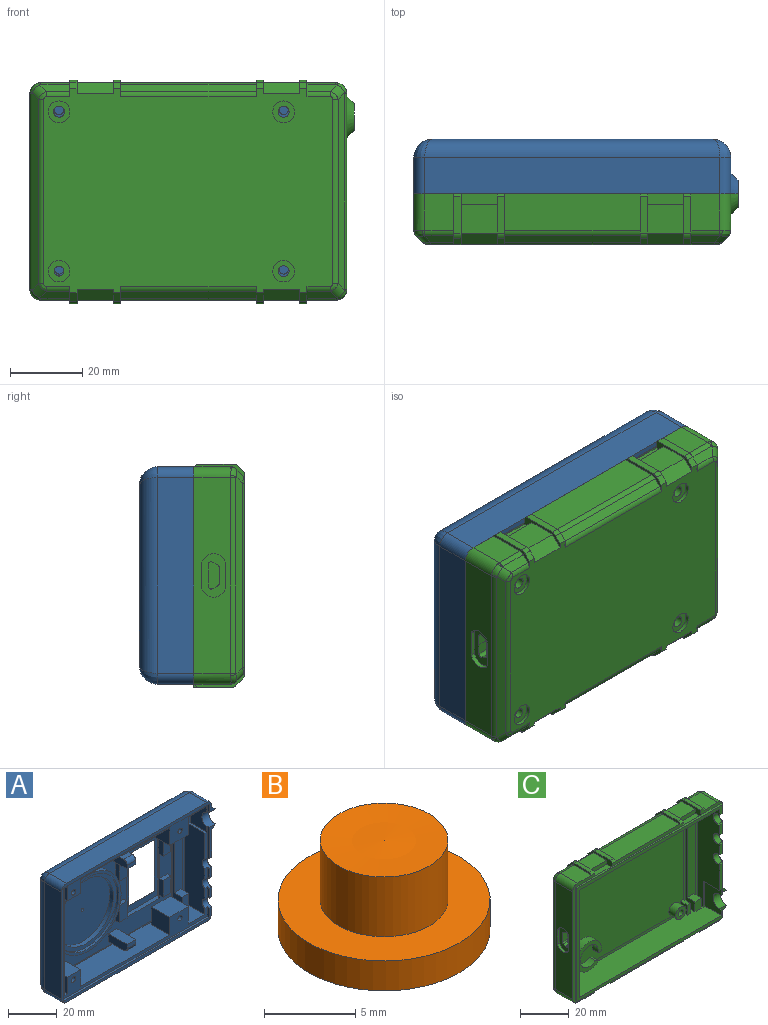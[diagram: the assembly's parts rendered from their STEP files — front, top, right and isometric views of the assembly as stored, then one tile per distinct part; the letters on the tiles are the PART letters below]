
ASSEMBLY  parts=3 mates=3
PART A: 134 faces, bbox 89.5x15x60 mm
  f0: plane 89.5x60mm, normal (0,-1,0), area 326.9mm2, adj f28,f29,f31,f46,f47,f50,f51,f56
  f1: plane 77.5x50mm, normal (0,1,0), area 3239.4mm2, adj f53,f113,f114,f115,f116,f122,f125,f126
  f2: plane 85x57mm, normal (0,-1,0), area 663.4mm2, adj f3,f4,f11,f12,f14,f15,f17,f18
  f3: plane 11x10.5mm, normal (0,0,-1), area 115.5mm2, adj f2,f8,f17,f112
  f4: plane 11x10.5mm, normal (0,0,1), area 115.5mm2, adj f2,f8,f18,f111
  f5: plane 11x2mm, normal (0,1,0), area 22mm2, adj f15,f16,f18,f111
  f6: plane 5x2mm, normal (0,-1,0), area 10mm2, adj f71,f72,f73,f75
  f7: plane 5x2mm, normal (0,-1,0), area 10mm2, adj f66,f67,f68,f70
  f8: plane 70.71x50mm, normal (0,-1,0), area 1324.2mm2, adj f3,f4,f10,f11,f12,f16,f17,f18
  f9: plane 32.22x20.2mm, normal (0,-1,0), area 258mm2, adj f10,f23,f92,f113,f114,f115,f116,f118
  f10: plane 20.2x2mm, normal (0,0,-1), area 39.9mm2, adj f8,f9,f92,f93,f117,f118
  f11: plane 10.5x7.6mm, normal (0,0,-1), area 79.8mm2, adj f2,f8,f83,f89,f91
  f12: plane 10.5x7.6mm, normal (0,0,1), area 79.8mm2, adj f2,f8,f13,f88,f90
  f13: plane 8.4x7.6mm, normal (0,1,0), area 18.3mm2, adj f12,f15,f16,f64,f88,f90
  f14: plane 81.5x12mm, normal (0,0,-1), area 782.7mm2, adj f2,f17,f26,f37,f65,f78,f83,f89
  f15: plane 81.5x12mm, normal (0,0,1), area 782.7mm2, adj f2,f5,f13,f18,f26,f37,f65,f88
  f16: plane 77.51x5.5mm, normal (0,0,-1), area 128.4mm2, adj f5,f8,f13,f24,f35,f39,f40,f41
  f17: plane 10.5x8.9mm, normal (-1,0,0), area 93.4mm2, adj f2,f3,f8,f14,f78
  f18: plane 10.5x8.9mm, normal (-1,0,0), area 93.4mm2, adj f2,f4,f5,f8,f15
  f19: plane 77.51x5.5mm, normal (0,0,1), area 128.4mm2, adj f8,f24,f35,f39,f43,f44,f52,f63
  f20: cylinder r=18mm len=36mm, axis (0,1,0), area 135.7mm2, adj f76,f77
  f21: cylinder r=19.25mm len=38.5mm, axis (0,1,0), area 326.6mm2, adj f8,f77
  f22: cylinder r=16mm len=32mm, axis (0,1,0), area 201.1mm2, adj f45,f76
  f23: plane 20.2x2mm, normal (0,0,1), area 39.9mm2, adj f8,f9,f92,f93,f117,f118
  f24: plane 50x1.3mm, normal (1,0,0), area 65mm2, adj f8,f16,f19,f52
  f25: plane 16.09x1.5mm, normal (0,-1,0), area 21.4mm2, adj f26,f48,f55,f57,f61,f62
  f26: plane 54x12mm, normal (-1,0,0), area 512.2mm2, adj f2,f14,f15,f25,f30,f36,f54,f55
  f27: plane 15.75x3.5mm, normal (0,-1,0), area 25.6mm2, adj f29,f48,f55,f57,f58
  f28: plane 4.39x1mm, normal (-1,0,0), area 4.3mm2, adj f0,f2,f47,f57
  f29: plane 54x10mm, normal (1,0,0), area 458.6mm2, adj f0,f27,f34,f49,f54,f55,f56,f58
  f30: plane 5.42x1.5mm, normal (0,-1,0), area 8.1mm2, adj f26,f32,f54,f55
  f31: plane 4.71x1mm, normal (-1,0,0), area 4.6mm2, adj f0,f2,f46,f56
  f32: plane 5.42x1mm, normal (-1,0,0), area 5.1mm2, adj f30,f34,f54,f55
  f33: plane 5.42x1mm, normal (-1,0,0), area 5.1mm2, adj f36,f49,f54,f56
  f34: plane 5x1.5mm, normal (0,-1,0), area 7.5mm2, adj f29,f32,f54,f55
  f35: plane 50x4.8mm, normal (0,-1,0), area 187.6mm2, adj f16,f19,f38,f39,f40,f42,f43,f63
  f36: plane 5.42x1.5mm, normal (0,-1,0), area 8.1mm2, adj f26,f33,f54,f56
  f37: plane 54x12mm, normal (1,0,0), area 648mm2, adj f2,f14,f15,f65
  f38: plane 4.5x3.8mm, normal (0,0,1), area 17.1mm2, adj f35,f39,f40,f41
  f39: plane 50x5.3mm, normal (-1,0,0), area 102.1mm2, adj f16,f19,f35,f38,f41,f42,f44,f52
  f40: plane 6.9x4.5mm, normal (1,0,0), area 31mm2, adj f16,f35,f38,f41
  f41: plane 6.9x3.8mm, normal (0,-1,0), area 26.2mm2, adj f16,f38,f39,f40
  f42: plane 4.5x3.8mm, normal (0,0,-1), area 17.1mm2, adj f35,f39,f43,f44
  f43: plane 6.9x4.5mm, normal (1,0,0), area 31mm2, adj f19,f35,f42,f44
  f44: plane 6.9x3.8mm, normal (0,-1,0), area 26.2mm2, adj f19,f39,f42,f43
  f45: plane 32x32mm, normal (0,-1,0), area 802.5mm2, adj f22,f53
  f46: plane 85x1mm, normal (0,0,1), area 85mm2, adj f0,f2,f31,f108
  f47: plane 85x1mm, normal (0,0,-1), area 85mm2, adj f0,f2,f28,f108
  f48: plane 16.09x1mm, normal (-1,0,0), area 15.9mm2, adj f25,f27,f55,f57
  f49: plane 5x1.5mm, normal (0,-1,0), area 7.5mm2, adj f29,f33,f54,f56
  f50: plane 81.5x10mm, normal (0,0,-1), area 815mm2, adj f0,f110,f120,f126
  f51: plane 81.5x10mm, normal (0,0,1), area 815mm2, adj f0,f109,f121,f125
  f52: plane 50x2mm, normal (0,-1,0), area 100mm2, adj f16,f19,f24,f39
  f53: cylinder r=0.75mm len=3mm, axis (0,-1,0), area 14.1mm2, adj f1,f45
  f54: cylinder r=2.5mm len=5mm, axis (1,0,0), area 20.5mm2, adj f26,f29,f30,f32,f33,f34,f36,f49
  f55: cylinder r=2.5mm len=5mm, axis (1,0,0), area 20.5mm2, adj f25,f26,f27,f29,f30,f32,f34,f48
  f56: cylinder r=2.5mm len=5mm, axis (1,0,0), area 20.5mm2, adj f0,f2,f26,f29,f31,f33,f36,f49
  f57: cylinder r=3.75mm len=7.5mm, axis (1,0,0), area 46.1mm2, adj f0,f2,f25,f27,f28,f48,f58,f62
  f58: cone r=3.75mm half-angle=45deg, axis (-1,0,0), area 42.2mm2, adj f0,f27,f29,f57
  f59: plane 9.5x1mm, normal (0,0,-1), area 9.5mm2, adj f2,f26,f60,f62
  f60: plane 12.73x1mm, normal (0,-1,0), area 12.7mm2, adj f26,f59,f61,f62
  f61: plane 9.5x1mm, normal (0,0,1), area 9.5mm2, adj f25,f26,f60,f62
  f62: plane 12.73x9.5mm, normal (-1,0,0), area 106.2mm2, adj f2,f25,f57,f59,f60,f61
  f63: plane 50x1mm, normal (1,0,0), area 50mm2, adj f16,f19,f35,f65
  f64: plane 50x1.5mm, normal (-1,0,0), area 75mm2, adj f8,f13,f16,f19,f65,f83
  f65: plane 81.5x54mm, normal (0,-1,0), area 525.5mm2, adj f14,f15,f16,f19,f26,f37,f63,f64
  f66: cylinder r=2mm len=5mm, axis (-1,0,0), area 15.7mm2, adj f7,f68,f69,f70
  f67: plane 11x5mm, normal (0,0,1), area 55mm2, adj f7,f8,f68,f70
  f68: plane 11x4mm, normal (1,0,0), area 43.1mm2, adj f7,f8,f66,f67,f69
  f69: plane 9x5mm, normal (0,0,-1), area 45mm2, adj f8,f66,f68,f70
  f70: plane 11x4mm, normal (-1,0,0), area 43.1mm2, adj f7,f8,f66,f67,f69
  f71: cylinder r=2mm len=5mm, axis (1,0,0), area 15.7mm2, adj f6,f73,f74,f75
  f72: plane 11x5mm, normal (0,0,-1), area 55mm2, adj f6,f8,f73,f75
  f73: plane 11x4mm, normal (-1,0,0), area 43.1mm2, adj f6,f8,f71,f72,f74
  f74: plane 9x5mm, normal (0,0,1), area 45mm2, adj f8,f71,f73,f75
  f75: plane 11x4mm, normal (1,0,0), area 43.1mm2, adj f6,f8,f71,f72,f74
  f76: plane 36x36mm, normal (0,-1,0), area 213.6mm2, adj f20,f22
  f77: plane 38.5x38.5mm, normal (0,-1,0), area 146.3mm2, adj f20,f21
  f78: plane 11x2mm, normal (0,1,0), area 22mm2, adj f14,f17,f19,f112
  f79: plane 2.5x2.5mm, normal (0,-1,0), area 4.9mm2, adj f80
  f80: cylinder r=1.25mm len=11mm, axis (0,1,0), area 86.4mm2, adj f2,f79
  f81: plane 2.5x2.5mm, normal (0,-1,0), area 4.9mm2, adj f82
  f82: cylinder r=1.25mm len=11mm, axis (0,1,0), area 86.4mm2, adj f2,f81
  f83: plane 7.6x7.1mm, normal (0,1,0), area 17.7mm2, adj f11,f14,f19,f64,f89,f91
  f84: plane 2.5x2.5mm, normal (0,-1,0), area 4.9mm2, adj f85
  f85: cylinder r=1.25mm len=11mm, axis (0,1,0), area 86.4mm2, adj f2,f84
  f86: plane 2.5x2.5mm, normal (0,-1,0), area 4.9mm2, adj f87
  f87: cylinder r=1.25mm len=11mm, axis (0,1,0), area 86.4mm2, adj f2,f86
  f88: plane 10.5x8.4mm, normal (-1,0,0), area 88.2mm2, adj f2,f12,f13,f15
  f89: plane 10.5x7.1mm, normal (-1,0,0), area 74.5mm2, adj f2,f11,f14,f83
  f90: plane 10.5x8.4mm, normal (1,0,0), area 88.2mm2, adj f2,f8,f12,f13,f15
  f91: plane 10.5x7.1mm, normal (1,0,0), area 74.5mm2, adj f2,f8,f11,f14,f83
  f92: plane 32.22x2mm, normal (1,0,0), area 64.4mm2, adj f8,f9,f10,f23
  f93: plane 32.22x2.5mm, normal (-1,0,0), area 50.1mm2, adj f8,f10,f23,f94,f96,f97,f99,f117
  f94: plane 4.5x2mm, normal (0,0,1), area 9mm2, adj f8,f93,f95,f96
  f95: plane 8.5x2mm, normal (1,0,0), area 17mm2, adj f8,f94,f96,f131
  f96: plane 8.5x4.5mm, normal (0,-1,0), area 38.2mm2, adj f93,f94,f95,f131
  f97: plane 4.5x2mm, normal (0,0,-1), area 9mm2, adj f8,f93,f98,f99
  f98: plane 8.5x2mm, normal (1,0,0), area 17mm2, adj f8,f97,f99,f132
  f99: plane 8.5x4.5mm, normal (0,-1,0), area 38.2mm2, adj f93,f97,f98,f132
  f100: plane 8.5x2mm, normal (1,0,0), area 17mm2, adj f8,f101,f103,f130
  f101: plane 4.61x2mm, normal (0,0,1), area 9.2mm2, adj f8,f100,f102,f103
  f102: plane 8.5x2mm, normal (-1,0,0), area 17mm2, adj f8,f101,f103,f130
  f103: plane 8.5x4.61mm, normal (0,-1,0), area 39.2mm2, adj f100,f101,f102,f130
  f104: plane 4.61x2mm, normal (0,0,-1), area 9.2mm2, adj f8,f105,f106,f107
  f105: plane 8.5x2mm, normal (1,0,0), area 17mm2, adj f8,f104,f107,f133
  f106: plane 8.5x2mm, normal (-1,0,0), area 17mm2, adj f8,f104,f107,f133
  f107: plane 8.5x4.61mm, normal (0,-1,0), area 39.2mm2, adj f104,f105,f106,f133
  f108: plane 57x1mm, normal (1,0,0), area 57mm2, adj f0,f2,f46,f47
  f109: cylinder r=3mm len=10mm, axis (0,1,0), area 47.1mm2, adj f0,f29,f51,f127
  f110: cylinder r=3mm len=10mm, axis (0,-1,0), area 47.1mm2, adj f0,f29,f50,f128
  f111: plane 10.5x8.9mm, normal (1,0,0), area 93.4mm2, adj f2,f4,f5,f8,f15
  f112: plane 10.5x8.9mm, normal (1,0,0), area 93.4mm2, adj f2,f3,f8,f14,f78
  f113: cylinder r=3mm len=31.29mm, axis (0,0,1), area 89.3mm2, adj f1,f9,f114,f115
  f114: cylinder r=3mm len=20.25mm, axis (1,0,0), area 54.6mm2, adj f1,f9,f113,f116
  f115: cylinder r=3mm len=20.25mm, axis (-1,0,0), area 54.6mm2, adj f1,f9,f113,f116
  f116: cylinder r=3mm len=31.29mm, axis (0,0,-1), area 89.3mm2, adj f1,f9,f114,f115
  f117: plane 32.22x1mm, normal (0,1,0), area 32.2mm2, adj f10,f23,f93,f118
  f118: plane 32.22x1.5mm, normal (-1,0,0), area 48.3mm2, adj f9,f10,f23,f117
  f119: plane 54x10mm, normal (-1,0,0), area 540mm2, adj f0,f120,f121,f122
  f120: cylinder r=3mm len=10mm, axis (0,1,0), area 47.1mm2, adj f0,f50,f119,f124
  f121: cylinder r=3mm len=10mm, axis (0,-1,0), area 47.1mm2, adj f0,f51,f119,f123
  f122: cylinder r=5mm len=54mm, axis (0,0,-1), area 412.7mm2, adj f1,f119,f123,f124
  f123: bspline ~6.03x5mm, area 24.5mm2, adj f121,f122,f125
  f124: bspline ~6.03x5mm, area 24.5mm2, adj f120,f122,f126
  f125: cylinder r=5mm len=81.5mm, axis (-1,0,0), area 628.7mm2, adj f1,f51,f123,f127
  f126: cylinder r=5mm len=81.5mm, axis (1,0,0), area 628.7mm2, adj f1,f50,f124,f128
  f127: bspline ~6.03x5mm, area 24.5mm2, adj f109,f125,f129
  f128: bspline ~6.03x5mm, area 24.5mm2, adj f110,f126,f129
  f129: cylinder r=5mm len=54mm, axis (0,0,1), area 412.7mm2, adj f1,f29,f127,f128
  f130: plane 4.61x2mm, normal (0,0,-1), area 9.2mm2, adj f8,f100,f102,f103
  f131: plane 4.5x2mm, normal (0,0,-1), area 9mm2, adj f8,f93,f95,f96
  f132: plane 4.5x2mm, normal (0,0,1), area 9mm2, adj f8,f93,f98,f99
  f133: plane 4.61x2mm, normal (0,0,1), area 9.2mm2, adj f8,f105,f106,f107
PART B: 7 faces, bbox 11.6x11.6x6 mm
  f0: plane 4x4mm, normal (0,0,-1), area 12.6mm2, adj f6
  f1: torus R=1.75mm, axis (0,0,1), area 38.5mm2, adj f2
  f2: cylinder r=3.5mm len=7mm, axis (0,0,1), area 88mm2, adj f1,f3
  f3: plane 11.6x11.6mm, normal (0,0,1), area 67.2mm2, adj f2,f4
  f4: cylinder r=5.8mm len=11.6mm, axis (0,0,1), area 72.9mm2, adj f3,f5
  f5: plane 11.6x11.6mm, normal (0,0,-1), area 93.1mm2, adj f4,f6
  f6: cylinder r=2mm len=4mm, axis (0,0,1), area 50.3mm2, adj f0,f5
PART C: 234 faces, bbox 89.5x15x61.7 mm
  f0: cylinder r=0.8mm len=3.7mm, axis (1,0,0), area 6mm2, adj f1,f8,f9,f233
  f1: plane 3.7x2.97mm, normal (0,1,-0.01), area 11mm2, adj f0,f2,f9,f233
  f2: plane 3.7x2.96mm, normal (0,1,0), area 10.9mm2, adj f1,f3,f9,f233
  f3: cylinder r=0.8mm len=3.7mm, axis (1,0,0), area 6.1mm2, adj f2,f4,f9,f233
  f4: plane 3.7x1.37mm, normal (0,-0.45,0.89), area 5.7mm2, adj f3,f5,f9,f233
  f5: cylinder r=0.81mm len=3.7mm, axis (1,0,0), area 3.3mm2, adj f4,f6,f9,f233
  f6: plane 4.51x3.7mm, normal (0,-1,0), area 16.7mm2, adj f5,f7,f9,f233
  f7: cylinder r=0.83mm len=3.7mm, axis (1,0,0), area 3.2mm2, adj f6,f8,f9,f233
  f8: plane 3.7x1.37mm, normal (0,-0.46,-0.89), area 5.7mm2, adj f0,f7,f9,f233
  f9: plane 14x9.5mm, normal (1,0,0), area 112.9mm2, adj f0,f1,f2,f3,f4,f5,f6,f7
  f10: plane 70.7x50mm, normal (0,-1,0), area 3334.4mm2, adj f9,f34,f61,f68,f72,f77,f82,f139
  f11: plane 14x2mm, normal (0,-1,0), area 28mm2, adj f9,f13,f14,f225
  f12: plane 5.01x2.01mm, normal (0,0,1), area 10mm2, adj f9,f14,f226,f227,f228
  f13: plane 4.01x2.01mm, normal (0,0,1), area 8mm2, adj f9,f11,f14,f228
  f14: plane 54x13mm, normal (1,0,0), area 555mm2, adj f11,f12,f13,f22,f55,f56,f225,f227
  f15: plane 5.5x4.8mm, normal (0,0,1), area 21.9mm2, adj f17,f76,f78,f79,f223,f227
  f16: plane 5.5x4.8mm, normal (0,0,-1), area 21.9mm2, adj f17,f78,f80,f83,f223,f227
  f17: plane 50x4.8mm, normal (0,-1,0), area 202mm2, adj f15,f16,f75,f76,f78,f80,f81,f223
  f18: plane 54x13mm, normal (-1,0,0), area 534mm2, adj f19,f22,f55,f56,f84,f85,f86,f151
  f19: plane 15.75x1.5mm, normal (0,-1,0), area 20.9mm2, adj f18,f23,f153,f154,f220,f222
  f20: cylinder r=3.75mm len=7.5mm, axis (1,0,0), area 47.1mm2, adj f21,f23,f27,f31,f219,f222
  f21: plane 1x0.5mm, normal (0,0,1), area 0.5mm2, adj f20,f22,f150,f222
  f22: plane 84.5x57mm, normal (0,-1,0), area 340.4mm2, adj f14,f18,f21,f55,f56,f146,f147,f148
  f23: plane 1x0.5mm, normal (0,0,-1), area 0.5mm2, adj f19,f20,f154,f222
  f24: plane 54x10.17mm, normal (1,0,0), area 467.9mm2, adj f27,f29,f30,f31,f32,f84,f85,f86
  f25: plane 10x8mm, normal (0,0,-1), area 80mm2, adj f40,f125,f132,f213
  f26: plane 10x8mm, normal (0,0,-1), area 80mm2, adj f41,f117,f120,f211
  f27: plane 15x5.75mm, normal (0,-1,0), area 25.9mm2, adj f20,f24,f59,f93,f116,f117,f149,f150
  f28: plane 41.5x1.5mm, normal (0,-1,0), area 62.2mm2, adj f38,f120,f121,f131,f132,f149
  f29: plane 5x1.5mm, normal (0,-1,0), area 7.5mm2, adj f24,f84,f85,f160
  f30: plane 5x1.5mm, normal (0,-1,0), area 7.5mm2, adj f24,f85,f86,f157
  f31: plane 15.75x3.5mm, normal (0,-1,0), area 25.6mm2, adj f20,f24,f86,f154,f219
  f32: plane 13x7mm, normal (0,-1,0), area 26.3mm2, adj f24,f57,f84,f97,f99,f100,f101,f146
  f33: plane 60x13mm, normal (0,-1,0), area 120.6mm2, adj f42,f45,f58,f91,f95,f108,f125,f126
  f34: cylinder r=3mm len=6mm, axis (0,1,0), area 74.8mm2, adj f10,f65,f139,f143,f144
  f35: plane 10x8mm, normal (0,0,1), area 80mm2, adj f44,f108,f111,f137
  f36: plane 10x8mm, normal (0,0,1), area 80mm2, adj f49,f100,f103,f135
  f37: plane 41.5x1.5mm, normal (0,-1,0), area 62.2mm2, adj f47,f103,f111,f147,f216,f217
  f38: plane 37.5x10.17mm, normal (0,0,-1), area 381.4mm2, adj f28,f122,f130,f191
  f39: plane 37.5x1.83mm, normal (0,0.71,-0.71), area 97mm2, adj f122,f130,f191,f192
  f40: plane 10x3mm, normal (0,0.71,-0.71), area 42.4mm2, adj f25,f54,f125,f132
  f41: plane 10x3mm, normal (0,0.71,-0.71), area 42.4mm2, adj f26,f54,f117,f120
  f42: plane 10.17x8mm, normal (0,0,-1), area 81.4mm2, adj f33,f91,f127,f172
  f43: plane 8.26x1.83mm, normal (0,0.71,-0.71), area 19.1mm2, adj f92,f127,f172,f173,f186
  f44: plane 10x3mm, normal (0,0.71,0.71), area 42.4mm2, adj f35,f54,f108,f111
  f45: plane 10.17x8mm, normal (0,0,1), area 81.4mm2, adj f33,f95,f107,f180
  f46: plane 8.26x1.83mm, normal (0,0.71,0.71), area 19.1mm2, adj f96,f107,f179,f180,f190
  f47: plane 37.5x10.17mm, normal (0,0,1), area 381.4mm2, adj f37,f104,f112,f198
  f48: plane 37.5x1.83mm, normal (0,0.71,0.71), area 97mm2, adj f104,f112,f197,f198
  f49: plane 10x3mm, normal (0,0.71,0.71), area 42.4mm2, adj f36,f54,f100,f103
  f50: cylinder r=3mm len=6mm, axis (0,1,0), area 18.8mm2, adj f54,f74
  f51: cylinder r=3mm len=6mm, axis (0,1,0), area 18.8mm2, adj f54,f70
  f52: cylinder r=3mm len=6mm, axis (0,1,0), area 18.8mm2, adj f54,f66
  f53: cylinder r=3mm len=6mm, axis (0,1,0), area 18.8mm2, adj f54,f63
  f54: plane 79.84x56.41mm, normal (0,1,0), area 4131.5mm2, adj f40,f41,f44,f49,f50,f51,f52,f53
  f55: plane 81.5x13mm, normal (0,0,-1), area 1059.5mm2, adj f14,f18,f22,f227
  f56: plane 82.5x13mm, normal (0,0,1), area 1069mm2, adj f14,f18,f22,f221,f222,f227
  f57: plane 10.17x8mm, normal (0,0,1), area 81.4mm2, adj f32,f97,f99,f171
  f58: plane 54x10.17mm, normal (-1,0,0), area 479.4mm2, adj f33,f91,f95,f176,f229,f230,f231,f232
  f59: plane 10.17x8mm, normal (0,0,-1), area 81.4mm2, adj f27,f93,f115,f163
  f60: cylinder r=1.35mm len=6mm, axis (0,1,0), area 50.9mm2, adj f62,f63
  f61: cylinder r=3mm len=6mm, axis (0,1,0), area 75.4mm2, adj f10,f62
  f62: plane 6x6mm, normal (0,-1,0), area 22.5mm2, adj f60,f61
  f63: plane 6x6mm, normal (0,1,0), area 22.5mm2, adj f53,f60
  f64: cylinder r=1.5mm len=6mm, axis (0,1,0), area 56.5mm2, adj f65,f66
  f65: plane 6x6mm, normal (0,-1,0), area 21.2mm2, adj f34,f64
  f66: plane 6x6mm, normal (0,1,0), area 21.2mm2, adj f52,f64
  f67: cylinder r=1.5mm len=6mm, axis (0,1,0), area 56.5mm2, adj f69,f70
  f68: cylinder r=3mm len=6mm, axis (0,1,0), area 75.4mm2, adj f10,f69
  f69: plane 6x6mm, normal (0,-1,0), area 21.2mm2, adj f67,f68
  f70: plane 6x6mm, normal (0,1,0), area 21.2mm2, adj f51,f67
  f71: cylinder r=1.5mm len=6mm, axis (0,1,0), area 56.5mm2, adj f73,f74
  f72: cylinder r=3mm len=6mm, axis (0,1,0), area 75.4mm2, adj f10,f73
  f73: plane 6x6mm, normal (0,-1,0), area 21.2mm2, adj f71,f72
  f74: plane 6x6mm, normal (0,1,0), area 21.2mm2, adj f50,f71
  f75: plane 4.5x3.8mm, normal (0,0,-1), area 17.1mm2, adj f17,f76,f78,f79
  f76: plane 5x4.5mm, normal (1,0,0), area 22.5mm2, adj f15,f17,f75,f79
  f77: plane 70.7x5mm, normal (0,0,1), area 78.3mm2, adj f10,f204,f205,f206,f226,f227
  f78: plane 50x5.5mm, normal (-1,0,0), area 95mm2, adj f15,f16,f17,f75,f79,f81,f83,f227
  f79: plane 5x3.8mm, normal (0,-1,0), area 19mm2, adj f15,f75,f76,f78
  f80: plane 5x4.5mm, normal (1,0,0), area 22.5mm2, adj f16,f17,f81,f83
  f81: plane 4.5x3.8mm, normal (0,0,1), area 17.1mm2, adj f17,f78,f80,f83
  f82: plane 70.7x5mm, normal (0,0,-1), area 78.3mm2, adj f10,f204,f208,f209,f224,f227
  f83: plane 5x3.8mm, normal (0,-1,0), area 19mm2, adj f16,f78,f80,f81
  f84: cylinder r=2.5mm len=5mm, axis (1,0,0), area 23.6mm2, adj f18,f24,f29,f32,f151,f161
  f85: cylinder r=2.5mm len=5mm, axis (1,0,0), area 23.6mm2, adj f18,f24,f29,f30,f155,f159
  f86: cylinder r=2.5mm len=5mm, axis (1,0,0), area 23.6mm2, adj f18,f24,f30,f31,f153,f156
  f87: plane 8.26x1.83mm, normal (0,0.71,-0.71), area 19.1mm2, adj f94,f115,f163,f164,f181
  f88: plane 54.52x1.83mm, normal (-0.71,0.71,0), area 136.4mm2, adj f92,f96,f175,f176,f177,f188
  f89: plane 54.52x1.83mm, normal (0.71,0.71,0), area 136.4mm2, adj f94,f98,f166,f167,f168,f183
  f90: plane 8.26x1.83mm, normal (0,0.71,0.71), area 19.1mm2, adj f98,f99,f170,f171,f185
  f91: cylinder r=3mm len=10.21mm, axis (0,1,0), area 48.1mm2, adj f33,f42,f58,f173,f174,f175
  f92: cylinder r=3mm len=3.92mm, axis (-0.58,-0.58,-0.58), area 9.8mm2, adj f43,f88,f174,f187
  f93: cylinder r=3mm len=10.21mm, axis (0,-1,0), area 48.1mm2, adj f24,f27,f59,f164,f165,f166
  f94: cylinder r=3mm len=3.92mm, axis (0.58,-0.58,-0.58), area 9.8mm2, adj f87,f89,f165,f182
  f95: cylinder r=3mm len=10.21mm, axis (0,-1,0), area 48.1mm2, adj f33,f45,f58,f177,f178,f179
  f96: cylinder r=3mm len=3.92mm, axis (0.58,0.58,-0.58), area 9.8mm2, adj f46,f88,f178,f189
  f97: cylinder r=3mm len=10.21mm, axis (0,1,0), area 48.1mm2, adj f24,f32,f57,f168,f169,f170
  f98: cylinder r=3mm len=3.92mm, axis (-0.58,0.58,-0.58), area 9.8mm2, adj f89,f90,f169,f184
  f99: plane 14x4.83mm, normal (1,0,0), area 14.1mm2, adj f32,f54,f57,f90,f101,f102,f171,f185
  f100: plane 14x4mm, normal (-1,0,0), area 19.9mm2, adj f32,f36,f49,f54,f101,f102,f135,f136
  f101: plane 10.17x2mm, normal (0,0,1), area 20.3mm2, adj f32,f99,f100,f202
  f102: plane 2.41x2.41mm, normal (0,0.71,0.71), area 6.8mm2, adj f54,f99,f100,f202
  f103: plane 14x4mm, normal (1,0,0), area 19.4mm2, adj f36,f37,f49,f54,f105,f106,f135,f136
  f104: plane 14x4.83mm, normal (-1,0,0), area 13.6mm2, adj f47,f48,f54,f105,f106,f197,f198,f201
  f105: plane 9.17x2mm, normal (0,0,1), area 18.3mm2, adj f103,f104,f201,f216
  f106: plane 2.41x2.41mm, normal (0,0.71,0.71), area 6.8mm2, adj f54,f103,f104,f201
  f107: plane 14x4.83mm, normal (-1,0,0), area 13.6mm2, adj f45,f46,f54,f109,f110,f180,f190,f199
  f108: plane 14x4mm, normal (1,0,0), area 19.4mm2, adj f33,f35,f44,f54,f109,f110,f137,f138
  f109: plane 9.17x2mm, normal (0,0,1), area 18.3mm2, adj f107,f108,f199,f218
  f110: plane 2.41x2.41mm, normal (0,0.71,0.71), area 6.8mm2, adj f54,f107,f108,f199
  f111: plane 14x4mm, normal (-1,0,0), area 19.4mm2, adj f35,f37,f44,f54,f113,f114,f137,f138
  f112: plane 14x4.83mm, normal (1,0,0), area 13.6mm2, adj f47,f48,f54,f113,f114,f197,f198,f200
  f113: plane 9.17x2mm, normal (0,0,1), area 18.3mm2, adj f111,f112,f200,f217
  f114: plane 2.41x2.41mm, normal (0,0.71,0.71), area 6.8mm2, adj f54,f111,f112,f200
  f115: plane 14x4.54mm, normal (1,0,0), area 11.6mm2, adj f54,f59,f87,f116,f118,f119,f163,f181
  f116: plane 2x0.71mm, normal (0,-0.71,-0.71), area 2mm2, adj f27,f115,f117,f118
  f117: plane 14x3.71mm, normal (-1,0,0), area 17.4mm2, adj f26,f27,f41,f54,f116,f118,f119,f196
  f118: plane 10.17x2mm, normal (0,0,-1), area 20.3mm2, adj f115,f116,f117,f196
  f119: plane 2x1.71mm, normal (0,0.71,-0.71), area 4.8mm2, adj f54,f115,f117,f196
  f120: plane 14x3.71mm, normal (1,0,0), area 17.4mm2, adj f26,f28,f41,f54,f121,f123,f124,f193
  f121: plane 2x0.71mm, normal (0,-0.71,-0.71), area 2mm2, adj f28,f120,f122,f123
  f122: plane 14x4.54mm, normal (-1,0,0), area 11.6mm2, adj f38,f39,f54,f121,f123,f124,f191,f192
  f123: plane 10.17x2mm, normal (0,0,-1), area 20.3mm2, adj f120,f121,f122,f193
  f124: plane 2x1.71mm, normal (0,0.71,-0.71), area 4.8mm2, adj f54,f120,f122,f193
  f125: plane 14x3.71mm, normal (1,0,0), area 17.4mm2, adj f25,f33,f40,f54,f126,f128,f129,f194
  f126: plane 2x0.71mm, normal (0,-0.71,-0.71), area 2mm2, adj f33,f125,f127,f128
  f127: plane 14x4.54mm, normal (-1,0,0), area 11.6mm2, adj f42,f43,f54,f126,f128,f129,f172,f186
  f128: plane 10.17x2mm, normal (0,0,-1), area 20.3mm2, adj f125,f126,f127,f194
  f129: plane 2x1.71mm, normal (0,0.71,-0.71), area 4.8mm2, adj f54,f125,f127,f194
  f130: plane 14x4.54mm, normal (1,0,0), area 11.6mm2, adj f38,f39,f54,f131,f133,f134,f191,f192
  f131: plane 2x0.71mm, normal (0,-0.71,-0.71), area 2mm2, adj f28,f130,f132,f133
  f132: plane 14x3.71mm, normal (-1,0,0), area 17.4mm2, adj f25,f28,f40,f54,f131,f133,f134,f195
  f133: plane 10.17x2mm, normal (0,0,-1), area 20.3mm2, adj f130,f131,f132,f195
  f134: plane 2x1.71mm, normal (0,0.71,-0.71), area 4.8mm2, adj f54,f130,f132,f195
  f135: plane 10x2mm, normal (0,-1,0), area 20mm2, adj f36,f100,f103,f136
  f136: plane 10x3mm, normal (0,0,1), area 30mm2, adj f100,f103,f135,f145
  f137: plane 10x2mm, normal (0,-1,0), area 20mm2, adj f35,f108,f111,f138
  f138: plane 10x3mm, normal (0,0,1), area 30mm2, adj f108,f111,f137,f152
  f139: cylinder r=7.2mm len=11.72mm, axis (0,1,0), area 48.7mm2, adj f10,f34,f140,f144
  f140: plane 3.5x1.85mm, normal (0.45,0,0.89), area 7.2mm2, adj f10,f139,f141,f144
  f141: cylinder r=5.25mm len=10.5mm, axis (0,1,0), area 103.1mm2, adj f10,f140,f142,f144
  f142: plane 3.5x1.98mm, normal (0,0,-1), area 6.9mm2, adj f10,f141,f143,f144
  f143: cylinder r=7.2mm len=14.4mm, axis (0,1,0), area 93.5mm2, adj f10,f34,f142,f144
  f144: plane 14.4x14.4mm, normal (0,-1,0), area 68.5mm2, adj f34,f139,f140,f141,f142,f143
  f145: plane 10x0.5mm, normal (0,1,0), area 5mm2, adj f100,f103,f136,f147
  f146: plane 4.5x1mm, normal (1,0,0), area 4.5mm2, adj f22,f32,f147,f151
  f147: plane 84.5x1mm, normal (0,0,1), area 84.5mm2, adj f22,f32,f33,f37,f145,f146,f148,f152
  f148: plane 57x1mm, normal (-1,0,0), area 57mm2, adj f22,f33,f147,f149
  f149: plane 84.5x1mm, normal (0,0,-1), area 84.5mm2, adj f22,f27,f28,f33,f148,f150,f210,f214
  f150: plane 4.25x1mm, normal (1,0,0), area 4.2mm2, adj f21,f22,f27,f149
  f151: plane 1.5x1mm, normal (0,0,-1), area 1.5mm2, adj f18,f22,f84,f146
  f152: plane 10x0.5mm, normal (0,1,0), area 5mm2, adj f108,f111,f138,f147
  f153: plane 1.5x1mm, normal (0,0,1), area 1.5mm2, adj f18,f19,f86,f154
  f154: plane 15.75x1mm, normal (1,0,0), area 15.7mm2, adj f19,f23,f31,f153
  f155: plane 1.5x1mm, normal (0,0,1), area 1.5mm2, adj f18,f85,f157,f158
  f156: plane 1.5x1mm, normal (0,0,-1), area 1.5mm2, adj f18,f86,f157,f158
  f157: plane 5x1mm, normal (1,0,0), area 5mm2, adj f30,f155,f156,f158
  f158: plane 5x1.5mm, normal (0,-1,0), area 7.5mm2, adj f18,f155,f156,f157
  f159: plane 1.5x1mm, normal (0,0,-1), area 1.5mm2, adj f18,f85,f160,f162
  f160: plane 5x1mm, normal (1,0,0), area 5mm2, adj f29,f159,f161,f162
  f161: plane 1.5x1mm, normal (0,0,1), area 1.5mm2, adj f18,f84,f160,f162
  f162: plane 5x1.5mm, normal (0,-1,0), area 7.5mm2, adj f18,f159,f160,f161
  f163: cylinder r=2mm len=8mm, axis (1,0,0), area 12.6mm2, adj f59,f87,f115,f164
  f164: bspline ~1.46x0.9mm, area 0.9mm2, adj f87,f93,f163,f165
  f165: bspline ~3x3mm, area 6mm2, adj f93,f94,f164,f166
  f166: bspline ~1.46x0.9mm, area 0.9mm2, adj f89,f93,f165,f167
  f167: cylinder r=2mm len=54mm, axis (0,0,1), area 84.8mm2, adj f24,f89,f166,f168
  f168: bspline ~1.46x1.03mm, area 0.9mm2, adj f89,f97,f167,f169
  f169: bspline ~3x3mm, area 6mm2, adj f97,f98,f168,f170
  f170: bspline ~1.46x1.42mm, area 0.9mm2, adj f90,f97,f169,f171
  f171: cylinder r=2mm len=8mm, axis (-1,0,0), area 12.6mm2, adj f57,f90,f99,f170
  f172: cylinder r=2mm len=8mm, axis (1,0,0), area 12.6mm2, adj f42,f43,f127,f173
  f173: bspline ~1.46x1.03mm, area 0.9mm2, adj f43,f91,f172,f174
  f174: bspline ~3x3mm, area 6mm2, adj f91,f92,f173,f175
  f175: bspline ~1.46x1.42mm, area 0.9mm2, adj f88,f91,f174,f176
  f176: cylinder r=2mm len=54mm, axis (0,0,-1), area 84.8mm2, adj f58,f88,f175,f177
  f177: bspline ~1.46x0.9mm, area 0.9mm2, adj f88,f95,f176,f178
  f178: bspline ~3x3mm, area 6mm2, adj f95,f96,f177,f179
  f179: bspline ~1.46x0.9mm, area 0.9mm2, adj f46,f95,f178,f180
  f180: cylinder r=2mm len=8mm, axis (-1,0,0), area 12.6mm2, adj f45,f46,f107,f179
  f181: cylinder r=2mm len=6.46mm, axis (-1,0,0), area 10.2mm2, adj f54,f87,f115,f182
  f182: bspline ~2.12x2.12mm, area 2.9mm2, adj f54,f94,f181,f183
  f183: cylinder r=2mm len=50.93mm, axis (0,0,1), area 80mm2, adj f54,f89,f182,f184
  f184: bspline ~2.12x2.12mm, area 2.9mm2, adj f54,f98,f183,f185
  f185: cylinder r=2mm len=6.46mm, axis (-1,0,0), area 10.2mm2, adj f54,f90,f99,f184
  f186: cylinder r=2mm len=6.46mm, axis (-1,0,0), area 10.2mm2, adj f43,f54,f127,f187
  f187: bspline ~2.12x2.12mm, area 2.9mm2, adj f54,f92,f186,f188
  f188: cylinder r=2mm len=50.93mm, axis (0,0,1), area 80mm2, adj f54,f88,f187,f189
  f189: bspline ~2.12x2.12mm, area 2.9mm2, adj f54,f96,f188,f190
  f190: cylinder r=2mm len=6.46mm, axis (-1,0,0), area 10.2mm2, adj f46,f54,f107,f189
  f191: cylinder r=2mm len=37.5mm, axis (1,0,0), area 58.9mm2, adj f38,f39,f122,f130
  f192: cylinder r=2mm len=37.5mm, axis (-1,0,0), area 58.9mm2, adj f39,f54,f122,f130
  f193: cylinder r=2mm len=2mm, axis (1,0,0), area 3.1mm2, adj f120,f122,f123,f124
  f194: cylinder r=2mm len=2mm, axis (1,0,0), area 3.1mm2, adj f125,f127,f128,f129
  f195: cylinder r=2mm len=2mm, axis (1,0,0), area 3.1mm2, adj f130,f132,f133,f134
  f196: cylinder r=2mm len=2mm, axis (1,0,0), area 3.1mm2, adj f115,f117,f118,f119
  f197: cylinder r=2mm len=37.5mm, axis (-1,0,0), area 58.9mm2, adj f48,f54,f104,f112
  f198: cylinder r=2mm len=37.5mm, axis (-1,0,0), area 58.9mm2, adj f47,f48,f104,f112
  f199: cylinder r=2mm len=2mm, axis (-1,0,0), area 3.1mm2, adj f107,f108,f109,f110
  f200: cylinder r=2mm len=2mm, axis (-1,0,0), area 3.1mm2, adj f111,f112,f113,f114
  f201: cylinder r=2mm len=2mm, axis (-1,0,0), area 3.1mm2, adj f103,f104,f105,f106
  f202: cylinder r=2mm len=2mm, axis (-1,0,0), area 3.1mm2, adj f99,f100,f101,f102
  f203: plane 4x1.9mm, normal (0,0,-1), area 7.6mm2, adj f10,f204,f205,f206
  f204: plane 50x5mm, normal (1,0,0), area 90mm2, adj f10,f77,f82,f203,f206,f207,f209,f227
  f205: plane 5x4mm, normal (-1,0,0), area 20mm2, adj f10,f77,f203,f206
  f206: plane 5x1.9mm, normal (0,-1,0), area 9.5mm2, adj f77,f203,f204,f205
  f207: plane 4x1.9mm, normal (0,0,1), area 7.6mm2, adj f10,f204,f208,f209
  f208: plane 5x4mm, normal (-1,0,0), area 20mm2, adj f10,f82,f207,f209
  f209: plane 5x1.9mm, normal (0,-1,0), area 9.5mm2, adj f82,f204,f207,f208
  f210: plane 10x0.5mm, normal (0,1,0), area 5mm2, adj f117,f120,f149,f212
  f211: plane 10x2mm, normal (0,-1,0), area 20mm2, adj f26,f117,f120,f212
  f212: plane 10x3mm, normal (0,0,-1), area 30mm2, adj f117,f120,f210,f211
  f213: plane 10x2mm, normal (0,-1,0), area 20mm2, adj f25,f125,f132,f215
  f214: plane 10x0.5mm, normal (0,1,0), area 5mm2, adj f125,f132,f149,f215
  f215: plane 10x3mm, normal (0,0,-1), area 30mm2, adj f125,f132,f213,f214
  f216: plane 2x1mm, normal (0,-0.71,0.71), area 2.8mm2, adj f37,f103,f104,f105
  f217: plane 2x1mm, normal (0,-0.71,0.71), area 2.8mm2, adj f37,f111,f112,f113
  f218: plane 2x1mm, normal (0,-0.71,0.71), area 2.8mm2, adj f33,f107,f108,f109
  f219: cone r=3.75mm half-angle=45deg, axis (-1,0,0), area 42.2mm2, adj f20,f24,f27,f31
  f220: plane 9.5x1mm, normal (0,0,-1), area 9.5mm2, adj f18,f19,f221,f222
  f221: plane 13x1mm, normal (0,-1,0), area 13mm2, adj f18,f56,f220,f222
  f222: plane 13x9.5mm, normal (-1,0,0), area 93.9mm2, adj f19,f20,f21,f22,f23,f56,f220,f221
  f223: plane 50x1mm, normal (1,0,0), area 50mm2, adj f15,f16,f17,f227
  f224: plane 18x1mm, normal (-1,0,0), area 18mm2, adj f10,f82,f225,f227
  f225: plane 10.5x2mm, normal (0,0,-1), area 21mm2, adj f9,f11,f14,f224,f227
  f226: plane 18x1mm, normal (-1,0,0), area 18mm2, adj f10,f12,f77,f227
  f227: plane 81.5x54mm, normal (0,-1,0), area 598mm2, adj f12,f14,f15,f16,f18,f55,f56,f77
  f228: plane 2.01x1.51mm, normal (0,0,1), area 3mm2, adj f9,f12,f13,f14
  f229: plane 7.34x1.3mm, normal (0,-1,0), area 9.5mm2, adj f58,f230,f232,f233
  f230: cylinder r=3.42mm len=6.5mm, axis (-1,0,0), area 11.1mm2, adj f58,f229,f231,f233
  f231: plane 7.33x1.3mm, normal (0,1,0), area 9.5mm2, adj f58,f230,f232,f233
  f232: cylinder r=3.44mm len=6.5mm, axis (-1,0,0), area 11.1mm2, adj f58,f229,f231,f233
  f233: plane 12x6.5mm, normal (-1,0,0), area 49.7mm2, adj f0,f1,f2,f3,f4,f5,f6,f7
PLACE A t=(-2.2,29.99,-29.56)mm
PLACE B rot(axis=(0,1,0),90deg) t=(37.55,14.99,-7.06)mm
PLACE C rot(axis=(-1,0,0),180deg) t=(-2.2,0.99,-29.56)mm
MATE planar A.f29 <-> C.f24  axis (1,0,0) through (41.55,14.99,-2.56)mm
MATE fastened A.f57 <-> B.f2  axis (-1,0,0) through (39.55,14.99,-9.06)mm
MATE planar C.f24 <-> A.f29  axis (1,0,0) through (41.55,14.99,-2.94)mm
